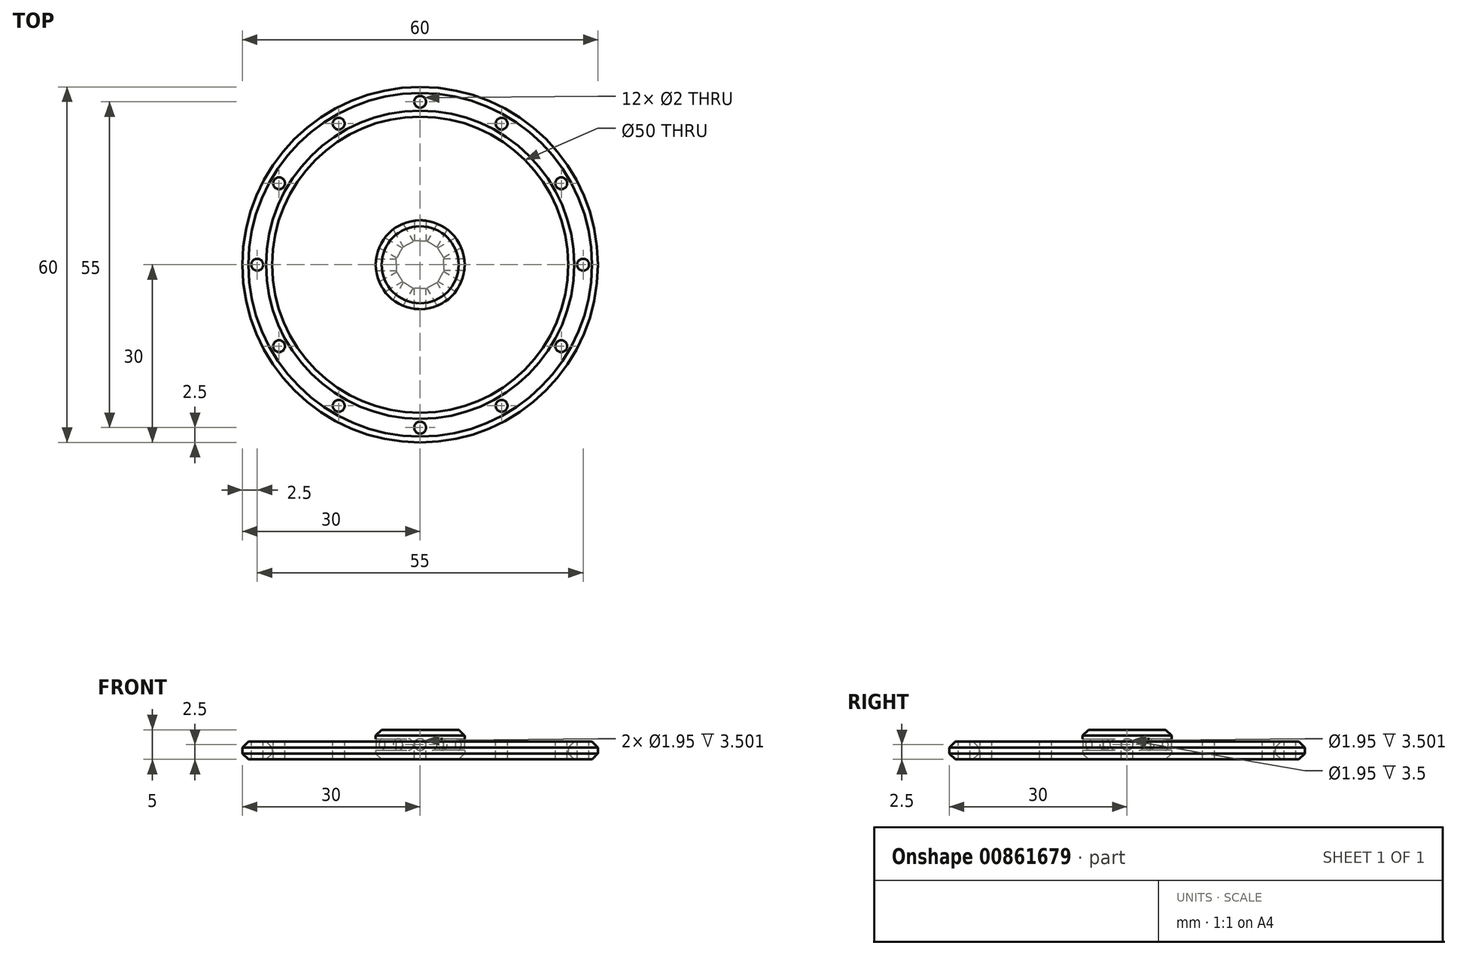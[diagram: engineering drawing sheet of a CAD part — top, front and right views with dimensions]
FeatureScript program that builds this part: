
annotation { "Feature Type Name" : "Feature", "Feature Type Description" : "" }
export const myFeature = defineFeature(function(context is Context, id is Id, definition is map)
    precondition{}
    {
        {
            var Q0;
            Q0=qCreatedBy(makeId("Top.planeOp"),FACE);
            var sketch = newSketch(context, id + "F0", { "sketchPlane" : qUnion([Q0])});
            skCircle(sketch, "E0", {"center": v(0, 0) * mm, "radius": 7.5 * mm});
            skCircle(sketch, "E1", {"center": v(0, 0) * mm, "radius": 25 * mm});
            skCircle(sketch, "E2.0", {"center": v(0, 0) * mm, "radius": 30 * mm});
            skLineSegment(sketch, "E3", {"start": v(0, 30) * mm, "end": v(0, 25) * mm});
            skPoint(sketch, "E4", {"position": v(0, 27.5) * mm});
            skSolve(sketch);
        }
        {
            var Q0;
            Q0=makeQuery(id+"F0.imprint","IMPRINT",FACE,{"disambiguationData":[TD([[makeQuery(id+"F0.imprint","IMPRINT",EDGE,{"derivedFrom":sQuery(id+"F0.wireOp",EDGE,"E1")}),-1.0]])]});
            extrude(context, id + "F1", {"entities" : qUnion([Q0]), "depth" : 3 * mm, "offsetDistance" : 25 * mm});
        }
        {
            var Q0;
            Q0=makeQuery(id+"F1.opExtrude","CAP_FACE",FACE,{"disambiguationData":[OSD([sQuery(id+"F0.wireOp",EDGE,"E1"),sQuery(id+"F0.wireOp",EDGE,"E2.0")])],"isStart":false});
            var sketch = newSketch(context, id + "F2", { "sketchPlane" : qUnion([Q0])});
            skLineSegment(sketch, "E5", {"start": v(0, 30) * mm, "end": v(0, 25) * mm});
            skPoint(sketch, "E6", {"position": v(0, 27.5) * mm});
            skPoint(sketch, "E7.center", {"position": v(0, 0) * mm});
            skPoint(sketch, "E8.1.0", {"position": v(-13.75, 23.82) * mm});
            skLineSegment(sketch, "E8.1.1", {"start": v(-15, 25.98) * mm, "end": v(-12.5, 21.65) * mm});
            skPoint(sketch, "E8.2.0", {"position": v(-23.82, 13.75) * mm});
            skLineSegment(sketch, "E8.2.1", {"start": v(-25.98, 15) * mm, "end": v(-21.65, 12.5) * mm});
            skPoint(sketch, "E8.3.0", {"position": v(-27.5, 0) * mm});
            skLineSegment(sketch, "E8.3.1", {"start": v(-30, 0) * mm, "end": v(-25, 0) * mm});
            skPoint(sketch, "E8.4.0", {"position": v(-23.82, -13.75) * mm});
            skLineSegment(sketch, "E8.4.1", {"start": v(-25.98, -15) * mm, "end": v(-21.65, -12.5) * mm});
            skPoint(sketch, "E8.5.0", {"position": v(-13.75, -23.82) * mm});
            skLineSegment(sketch, "E8.5.1", {"start": v(-15, -25.98) * mm, "end": v(-12.5, -21.65) * mm});
            skPoint(sketch, "E8.6.0", {"position": v(0, -27.5) * mm});
            skLineSegment(sketch, "E8.6.1", {"start": v(0, -30) * mm, "end": v(0, -25) * mm});
            skPoint(sketch, "E8.7.0", {"position": v(13.75, -23.82) * mm});
            skLineSegment(sketch, "E8.7.1", {"start": v(15, -25.98) * mm, "end": v(12.5, -21.65) * mm});
            skPoint(sketch, "E8.8.0", {"position": v(23.82, -13.75) * mm});
            skLineSegment(sketch, "E8.8.1", {"start": v(25.98, -15) * mm, "end": v(21.65, -12.5) * mm});
            skPoint(sketch, "E8.9.0", {"position": v(27.5, 0) * mm});
            skLineSegment(sketch, "E8.9.1", {"start": v(30, 0) * mm, "end": v(25, 0) * mm});
            skPoint(sketch, "E8.10.0", {"position": v(23.82, 13.75) * mm});
            skLineSegment(sketch, "E8.10.1", {"start": v(25.98, 15) * mm, "end": v(21.65, 12.5) * mm});
            skPoint(sketch, "E8.11.0", {"position": v(13.75, 23.82) * mm});
            skLineSegment(sketch, "E8.11.1", {"start": v(15, 25.98) * mm, "end": v(12.5, 21.65) * mm});
            skLineSegment(sketch, "E8.anchor1", {"start": v(0, 0) * mm, "end": v(0, 27.5) * mm, "construction": true});
            skLineSegment(sketch, "E8.anchor2", {"start": v(0, 0) * mm, "end": v(13.75, 23.82) * mm, "construction": true});
            skSolve(sketch);
        }
        {
            var Q0;
            Q0=sQuery(id+"F2.wireOp",VERTEX,"E6");
            var Q1;
            Q1=sQuery(id+"F2.wireOp",VERTEX,"E8.1.0");
            var Q2;
            Q2=sQuery(id+"F2.wireOp",VERTEX,"E8.2.0");
            var Q3;
            Q3=sQuery(id+"F2.wireOp",VERTEX,"E8.3.0");
            var Q4;
            Q4=sQuery(id+"F2.wireOp",VERTEX,"E8.4.0");
            var Q5;
            Q5=sQuery(id+"F2.wireOp",VERTEX,"E8.5.0");
            var Q6;
            Q6=sQuery(id+"F2.wireOp",VERTEX,"E8.6.0");
            var Q7;
            Q7=sQuery(id+"F2.wireOp",VERTEX,"E8.7.0");
            var Q8;
            Q8=sQuery(id+"F2.wireOp",VERTEX,"E8.8.0");
            var Q9;
            Q9=sQuery(id+"F2.wireOp",VERTEX,"E8.9.0");
            var Q10;
            Q10=sQuery(id+"F2.wireOp",VERTEX,"E8.10.0");
            var Q11;
            Q11=sQuery(id+"F2.wireOp",VERTEX,"E8.11.0");
            var Q12;
            Q12=makeQuery(id+"F1.opExtrude","SWEPT_BODY",BODY,{"disambiguationData":[OSD([sQuery(id+"F0.wireOp",EDGE,"E1"),sQuery(id+"F0.wireOp",EDGE,"E2.0")])]});
            hole(context, id + "F3", {"style" : HoleStyle.SIMPLE, "endStyle" : HoleEndStyle.THROUGH, "holeDiameter" : 2 * mm, "majorDiameter" : 5 * mm, "isTappedThrough" : true, "tappedDepth" : 12 * mm, "tapClearance" : 3, "locations" : qUnion([Q0, Q1, Q2, Q3, Q4, Q5, Q6, Q7, Q8, Q9, Q10, Q11]), "scope" : qUnion([Q12])});
        }
        {
            var Q0;
            Q0=makeQuery(id+"F1.opExtrude","CAP_EDGE",EDGE,{"disambiguationData":[OSD([sQuery(id+"F0.wireOp",EDGE,"E2.0")])],"isStart":false});
            var Q1;
            Q1=makeQuery(id+"F1.opExtrude","CAP_EDGE",EDGE,{"disambiguationData":[OSD([sQuery(id+"F0.wireOp",EDGE,"E1")])],"isStart":false});
            var Q2;
            Q2=makeQuery(id+"F1.opExtrude","CAP_EDGE",EDGE,{"disambiguationData":[OSD([sQuery(id+"F0.wireOp",EDGE,"E2.0")])],"isStart":true});
            var Q3;
            Q3=makeQuery(id+"F1.opExtrude","CAP_EDGE",EDGE,{"disambiguationData":[OSD([sQuery(id+"F0.wireOp",EDGE,"E1")])],"isStart":true});
            chamfer(context, id + "F4", {"entities" : qUnion([Q0, Q1, Q2, Q3]), "width" : 1 * mm, "tangentPropagation" : true});
        }
        {
            var Q0;
            Q0=makeQuery(id+"F0.imprint","IMPRINT",FACE,{"disambiguationData":[TD([[makeQuery(id+"F0.imprint","IMPRINT",EDGE,{"derivedFrom":sQuery(id+"F0.wireOp",EDGE,"E0")}),1.0]])]});
            extrude(context, id + "F5", {"entities" : qUnion([Q0]), "depth" : 5 * mm, "offsetDistance" : 25 * mm});
        }
        {
            var Q0;
            Q0=qCreatedBy(makeId("Front.planeOp"),FACE);
            var sketch = newSketch(context, id + "F6", { "sketchPlane" : qUnion([Q0])});
            skLineSegment(sketch, "E9", {"start": v(0, 0) * mm, "end": v(0, 5) * mm});
            skCircle(sketch, "E10", {"center": v(0, 2.5) * mm, "radius": 0.97 * mm});
            skSolve(sketch);
        }
        {
            var Q0;
            Q0 = qSketchRegion(id + "F6", true);
            var Q1;
            Q1=sQuery(id+"F6.wireOp",EDGE,"E10");
            extrude(context, id + "F7", {"entities" : qUnion([Q0]), "surfaceEntities" : qUnion([Q1]), "depth" : 14 * mm, "offsetDistance" : 25 * mm, "hasSecondDirection" : true, "secondDirectionOppositeDirection" : false, "secondDirectionDepth" : 4 * mm});
        }
        {
            var Q0;
            Q0=makeQuery(id+"F7.opExtrude","SWEPT_BODY",BODY,{"disambiguationData":[OSD([sQuery(id+"F6.wireOp",EDGE,"E10")])]});
            var Q1;
            Q1=sQuery(id+"F6.wireOp",EDGE,"E9");
            circularPattern(context, id + "F8", {"operationType" : NewBodyOperationType.REMOVE, "entities" : qUnion([Q0]), "axis" : qUnion([Q1]), "angle" : 360 * degree, "instanceCount" : 12, "equalSpace" : true});
        }
        {
            var Q0;
            Q0=makeQuery(id+"F5.opExtrude","CAP_EDGE",EDGE,{"disambiguationData":[OSD([sQuery(id+"F0.wireOp",EDGE,"E0")])],"isStart":false});
            var Q1;
            Q1=makeQuery(id+"F5.opExtrude","CAP_EDGE",EDGE,{"disambiguationData":[OSD([sQuery(id+"F0.wireOp",EDGE,"E0")])],"isStart":true});
            chamfer(context, id + "F9", {"entities" : qUnion([Q0, Q1]), "width" : 1 * mm, "tangentPropagation" : true});
        }
    });
